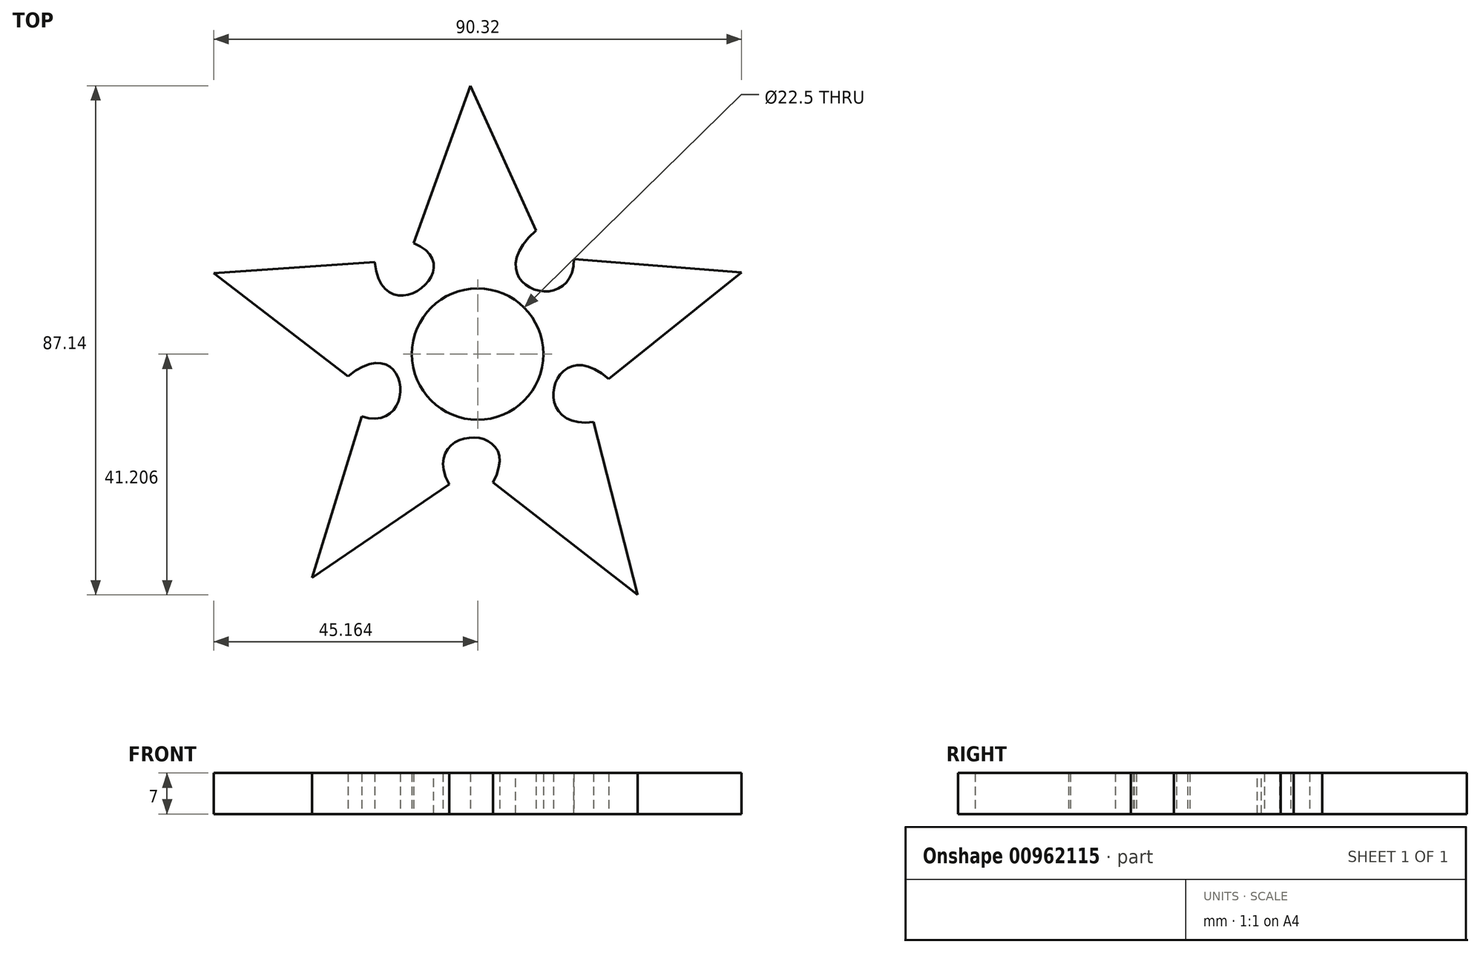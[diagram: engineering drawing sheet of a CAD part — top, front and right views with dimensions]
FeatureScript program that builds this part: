
annotation { "Feature Type Name" : "Feature", "Feature Type Description" : "" }
export const myFeature = defineFeature(function(context is Context, id is Id, definition is map)
    precondition{}
    {
        {
            var Q0;
            Q0=qCreatedBy(makeId("Top.planeOp"),FACE);
            var sketch = newSketch(context, id + "F0", { "sketchPlane" : qUnion([Q0])});
            skLineSegment(sketch, "E0", {"start": v(-6.7, 8.4) * mm, "end": v(3.05, 35.33) * mm});
            skLineSegment(sketch, "E1", {"start": v(3.05, 35.33) * mm, "end": v(14.26, 10.58) * mm});
            skLineSegment(sketch, "E2", {"start": v(-13.34, 5.16) * mm, "end": v(-40.87, 3.23) * mm});
            skLineSegment(sketch, "E3", {"start": v(-40.87, 3.23) * mm, "end": v(-17.94, -14.38) * mm});
            skFitSpline(sketch, "E4", {"points": [v(-13.34, 5.16) * mm, v(-6.7, 8.4) * mm], "startDerivative": vector(3.97, -38.29) * mm, "endDerivative": vector(-30.8, 12.44) * mm});
            skLineSegment(sketch, "E5", {"start": v(20.77, 5.69) * mm, "end": v(49.45, 3.4) * mm});
            skLineSegment(sketch, "E6", {"start": v(49.45, 3.4) * mm, "end": v(26.73, -14.83) * mm});
            skFitSpline(sketch, "E7", {"points": [v(14.26, 10.58) * mm, v(20.77, 5.69) * mm], "startDerivative": vector(-31.86, -28.9) * mm, "endDerivative": vector(-0.4, 31.13) * mm});
            skLineSegment(sketch, "E8", {"start": v(-15.58, -21.26) * mm, "end": v(-24.04, -48.89) * mm});
            skLineSegment(sketch, "E9", {"start": v(-24.04, -48.89) * mm, "end": v(-0.58, -32.87) * mm});
            skFitSpline(sketch, "E10", {"points": [v(-17.94, -14.38) * mm, v(-15.58, -21.26) * mm], "startDerivative": vector(32.2, 25.63) * mm, "endDerivative": vector(-29.71, 9.66) * mm});
            skLineSegment(sketch, "E11", {"start": v(6.9, -32.58) * mm, "end": v(31.72, -51.8) * mm});
            skLineSegment(sketch, "E12", {"start": v(31.72, -51.8) * mm, "end": v(24.15, -22.22) * mm});
            skFitSpline(sketch, "E13", {"points": [v(-0.58, -32.87) * mm, v(6.9, -32.58) * mm], "startDerivative": vector(-16.83, 30.5) * mm, "endDerivative": vector(-17.69, -32.2) * mm});
            skFitSpline(sketch, "E14", {"points": [v(24.15, -22.22) * mm, v(26.73, -14.83) * mm], "startDerivative": vector(-34.86, -4.95) * mm, "endDerivative": vector(28.87, -25.56) * mm});
            skCircle(sketch, "E15", {"center": v(4.3, -10.6) * mm, "radius": 11.25 * mm});
            skSolve(sketch);
        }
        {
            var Q0;
            Q0=makeQuery(id+"F0.imprint","IMPRINT",FACE,{"disambiguationData":[TD([[makeQuery(id+"F0.imprint","IMPRINT",EDGE,{"derivedFrom":sQuery(id+"F0.wireOp",EDGE,"E0")}),-1.0]])]});
            extrude(context, id + "F1", {"entities" : qUnion([Q0]), "depth" : 7 * mm, "offsetDistance" : 25 * mm});
        }
    });
